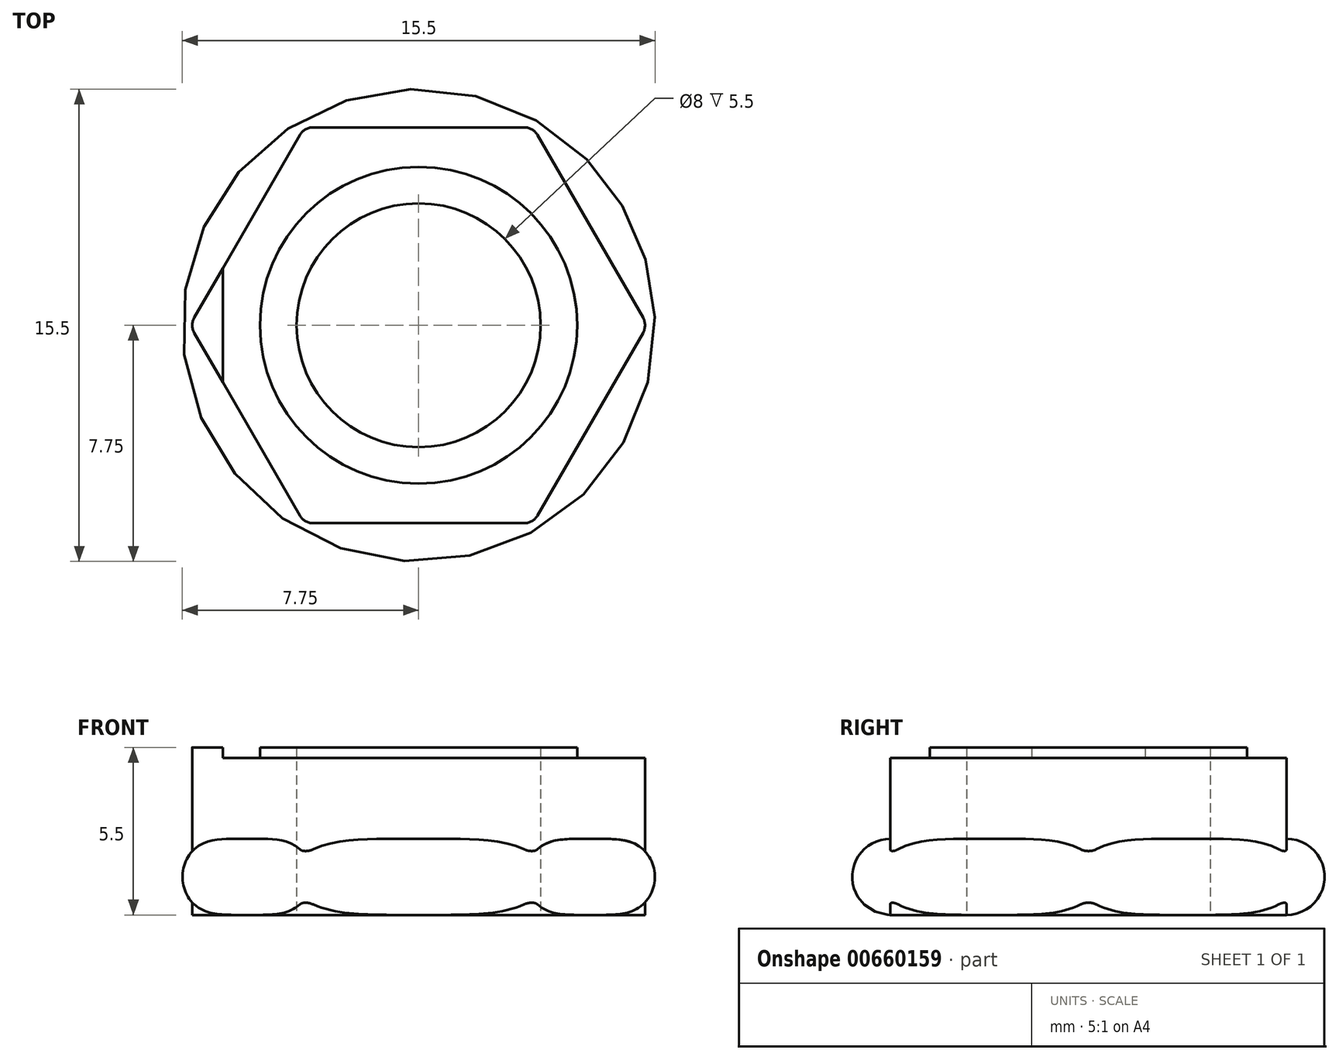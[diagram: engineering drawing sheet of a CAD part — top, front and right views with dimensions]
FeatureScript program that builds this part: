
annotation { "Feature Type Name" : "Feature", "Feature Type Description" : "" }
export const myFeature = defineFeature(function(context is Context, id is Id, definition is map)
    precondition{}
    {
        {
            var Q0;
            Q0=qCreatedBy(makeId("Top.planeOp"),FACE);
            var sketch = newSketch(context, id + "F0", { "sketchPlane" : qUnion([Q0])});
            skCircle(sketch, "E0.cCircle", {"center": v(0, 0) * mm, "radius": 6.5 * mm, "construction": true});
            skLineSegment(sketch, "E0.0", {"start": v(-3.75, 6.5) * mm, "end": v(3.75, 6.5) * mm});
            skLineSegment(sketch, "E0.1", {"start": v(3.75, 6.5) * mm, "end": v(7.5, 0) * mm});
            skLineSegment(sketch, "E0.2", {"start": v(7.5, 0) * mm, "end": v(3.75, -6.5) * mm});
            skLineSegment(sketch, "E0.3", {"start": v(3.75, -6.5) * mm, "end": v(-3.75, -6.5) * mm});
            skLineSegment(sketch, "E0.4", {"start": v(-3.75, -6.5) * mm, "end": v(-7.5, 0) * mm});
            skLineSegment(sketch, "E0.5", {"start": v(-7.5, 0) * mm, "end": v(-3.75, 6.5) * mm});
            skPoint(sketch, "E0.0.midPoint", {"position": v(0, 6.5) * mm});
            skCircle(sketch, "E1", {"center": v(0, 0) * mm, "radius": 4 * mm});
            skSolve(sketch);
        }
        {
            var Q0;
            Q0=makeQuery(id+"F0.imprint","IMPRINT",FACE,{"disambiguationData":[TD([[makeQuery(id+"F0.imprint","IMPRINT",EDGE,{"derivedFrom":sQuery(id+"F0.wireOp",EDGE,"E0.0")}),-1.0]])]});
            extrude(context, id + "F1", {"entities" : qUnion([Q0]), "depth" : (5.5 - .35) * mm});
        }
        {
            var Q0;
            Q0=makeQuery(id+"F1.opExtrude","SWEPT_EDGE",EDGE,{"disambiguationData":[OSD([sQuery(id+"F0.wireOp",EDGE,"E0.2"),sQuery(id+"F0.wireOp",EDGE,"E0.3")])]});
            var Q1;
            Q1=makeQuery(id+"F1.opExtrude","SWEPT_EDGE",EDGE,{"disambiguationData":[OSD([sQuery(id+"F0.wireOp",EDGE,"E0.1"),sQuery(id+"F0.wireOp",EDGE,"E0.2")])]});
            var Q2;
            Q2=makeQuery(id+"F1.opExtrude","SWEPT_EDGE",EDGE,{"disambiguationData":[OSD([sQuery(id+"F0.wireOp",EDGE,"E0.0"),sQuery(id+"F0.wireOp",EDGE,"E0.1")])]});
            var Q3;
            Q3=makeQuery(id+"F1.opExtrude","SWEPT_EDGE",EDGE,{"disambiguationData":[OSD([sQuery(id+"F0.wireOp",EDGE,"E0.0"),sQuery(id+"F0.wireOp",EDGE,"E0.5")])]});
            var Q4;
            Q4=makeQuery(id+"F1.opExtrude","SWEPT_EDGE",EDGE,{"disambiguationData":[OSD([sQuery(id+"F0.wireOp",EDGE,"E0.4"),sQuery(id+"F0.wireOp",EDGE,"E0.5")])]});
            var Q5;
            Q5=makeQuery(id+"F1.opExtrude","SWEPT_EDGE",EDGE,{"disambiguationData":[OSD([sQuery(id+"F0.wireOp",EDGE,"E0.3"),sQuery(id+"F0.wireOp",EDGE,"E0.4")])]});
            fillet(context, id + "F2", {"entities" : qUnion([Q0, Q1, Q2, Q3, Q4, Q5]), "radius" : .5 * mm, "tangentPropagation" : true, "allowEdgeOverflow" : false});
        }
        {
            var Q0;
            Q0=makeQuery(id+"F1.opExtrude","CAP_FACE",FACE,{"disambiguationData":[OSD([sQuery(id+"F0.wireOp",EDGE,"E0.0"),sQuery(id+"F0.wireOp",EDGE,"E0.1"),sQuery(id+"F0.wireOp",EDGE,"E0.2"),sQuery(id+"F0.wireOp",EDGE,"E0.3"),sQuery(id+"F0.wireOp",EDGE,"E0.4"),sQuery(id+"F0.wireOp",EDGE,"E0.5"),sQuery(id+"F0.wireOp",EDGE,"E1")])],"isStart":false});
            var sketch = newSketch(context, id + "F3", { "sketchPlane" : qUnion([Q0])});
            skLineSegment(sketch, "E2.0", {"start": v(-7.36, 0.25) * mm, "end": v(-3.9, 6.25) * mm});
            skLineSegment(sketch, "E3.0", {"start": v(-3.9, -6.25) * mm, "end": v(-7.36, -0.25) * mm});
            skPoint(sketch, "E4.0", {"position": v(-7.42, 0) * mm});
            skLineSegment(sketch, "E5", {"start": v(-6.42, 1.87) * mm, "end": v(-6.42, -1.87) * mm});
            skCircle(sketch, "E6", {"center": v(0, 0) * mm, "radius": 5.2 * mm});
            skSolve(sketch);
        }
        {
            var Q0;
            {var subQ4=sQuery(id+"F3.wireOp",EDGE,"E5");Q0=makeQuery(id+"F3.imprint","IMPRINT",FACE,{"disambiguationData":[TD([[makeQuery(id+"F3.imprint","IMPRINT",EDGE,{"derivedFrom":subQ4}),-1.0]])]});}
            extrude(context, id + "F4", {"entities" : qUnion([Q0]), "operationType" : NewBodyOperationType.ADD, "depth" : .35 * mm});
        }
        {
            var Q0;
            Q0=makeQuery(id+"F3.imprint","IMPRINT",FACE,{"disambiguationData":[TD([[makeQuery(id+"F3.imprint","IMPRINT",EDGE,{"derivedFrom":sQuery(id+"F3.wireOp",EDGE,"E6")}),1.0]])]});
            var Q1;
            Q1=makeQuery(id+"F4.opExtrude","CAP_FACE",FACE,{"disambiguationData":[OSD([sQuery(id+"F0.wireOp",EDGE,"E0.0"),sQuery(id+"F0.wireOp",EDGE,"E0.1"),sQuery(id+"F0.wireOp",EDGE,"E0.2"),sQuery(id+"F0.wireOp",EDGE,"E0.3"),sQuery(id+"F0.wireOp",EDGE,"E0.4"),sQuery(id+"F0.wireOp",EDGE,"E0.5"),sQuery(id+"F0.wireOp",EDGE,"E1"),sQuery(id+"F3.wireOp",EDGE,"E2.0"),sQuery(id+"F3.wireOp",EDGE,"E3.0"),sQuery(id+"F3.wireOp",EDGE,"E5")])],"isStart":false});
            extrude(context, id + "F5", {"entities" : qUnion([Q0]), "operationType" : NewBodyOperationType.ADD, "endBound" : BoundingType.UP_TO_SURFACE, "endBoundEntityFace" : qUnion([Q1]), "depth" : 25 * mm});
        }
        {
            var Q0;
            Q0=qCreatedBy(makeId("Right.planeOp"),FACE);
            var sketch = newSketch(context, id + "F6", { "sketchPlane" : qUnion([Q0])});
            skLineSegment(sketch, "E7.0", {"start": v(-6.5, 0) * mm, "end": v(-6.5, 5.5) * mm});
            skCircle(sketch, "E8", {"center": v(-6.5, 1.25) * mm, "radius": 1.25 * mm});
            skLineSegment(sketch, "E9", {"start": v(0, 0) * mm, "end": v(0, -1.28) * mm, "construction": true});
            skSolve(sketch);
        }
        {
            var Q0;
            {var subQ0=sQuery(id+"F6.wireOp",EDGE,"E8");var subQ1=sQuery(id+"F6.wireOp",EDGE,"E7.0");var subQ2=makeQuery(id+"F6.imprint","INTERSECT",VERTEX,{"disambiguationData":[OD(0.0)],"derivedFrom":[subQ1,subQ0]});Q0=makeQuery(id+"F6.imprint","IMPRINT",FACE,{"disambiguationData":[TD([[makeQuery(id+"F6.imprint","IMPRINT",EDGE,{"disambiguationData":[TD([[subQ2,-1.0]])],"derivedFrom":subQ1}),1.0]])]});}
            var Q1;
            Q1=sQuery(id+"F6.wireOp",EDGE,"E9");
            revolve(context, id + "F7", {"operationType" : NewBodyOperationType.ADD, "entities" : qUnion([Q0]), "axis" : qUnion([Q1]), "revolveType" : RevolveType.FULL});
        }
    });
